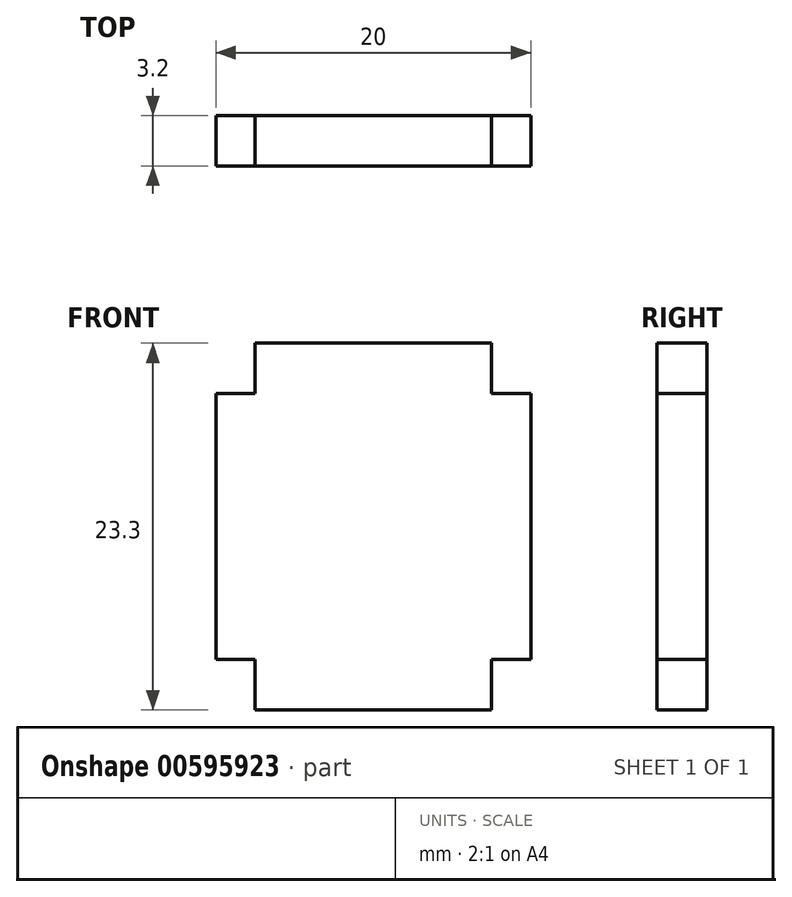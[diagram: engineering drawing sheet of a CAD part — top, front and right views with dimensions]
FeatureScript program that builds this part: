
annotation { "Feature Type Name" : "Feature", "Feature Type Description" : "" }
export const myFeature = defineFeature(function(context is Context, id is Id, definition is map)
    precondition{}
    {
        {
            var Q0;
            Q0=qCreatedBy(makeId("Front.planeOp"),FACE);
            var sketch = newSketch(context, id + "F0", { "sketchPlane" : qUnion([Q0])});
            skLineSegment(sketch, "E0.bottom", {"start": v(-10, 5.1) * mm, "end": v(10, 5.1) * mm});
            skLineSegment(sketch, "E0.top", {"start": v(-10, -11.8) * mm, "end": v(10, -11.8) * mm});
            skLineSegment(sketch, "E0.left", {"start": v(-10, 5.1) * mm, "end": v(-10, -11.8) * mm});
            skLineSegment(sketch, "E0.right", {"start": v(10, 5.1) * mm, "end": v(10, -11.8) * mm});
            skLineSegment(sketch, "E1", {"start": v(-7.5, -11.8) * mm, "end": v(-7.5, -15) * mm});
            skLineSegment(sketch, "E2", {"start": v(-7.5, 5.1) * mm, "end": v(-7.5, 8.3) * mm});
            skLineSegment(sketch, "E3", {"start": v(-7.5, 8.3) * mm, "end": v(7.5, 8.3) * mm});
            skLineSegment(sketch, "E4", {"start": v(7.5, 8.3) * mm, "end": v(7.5, 5.1) * mm});
            skLineSegment(sketch, "E5", {"start": v(7.5, -15) * mm, "end": v(7.5, -11.79) * mm});
            skLineSegment(sketch, "E6", {"start": v(-7.5, -15) * mm, "end": v(7.5, -15) * mm});
            skSolve(sketch);
        }
        {
            var Q0;
            Q0 = qSketchRegion(id + "F0", true);
            extrude(context, id + "F1", {"entities" : qUnion([Q0]), "depth" : 3.2 * mm, "offsetDistance" : 25 * mm});
        }
    });
